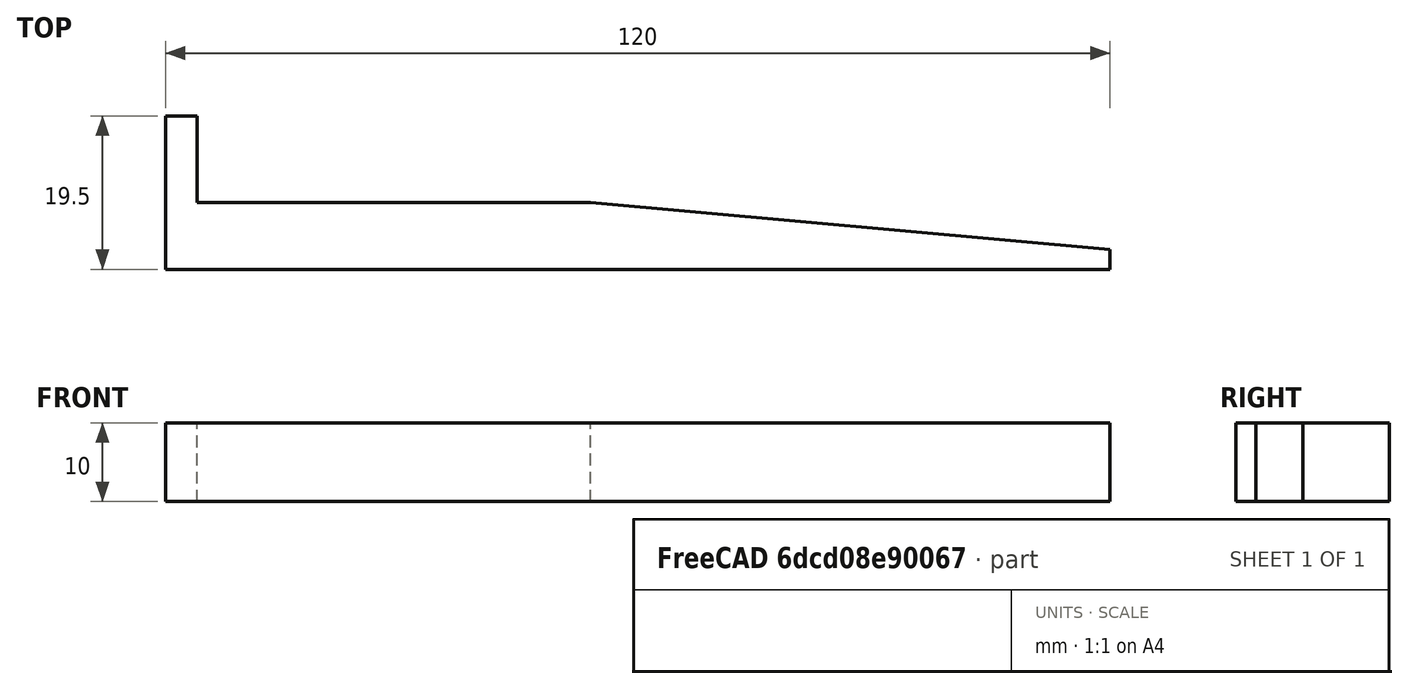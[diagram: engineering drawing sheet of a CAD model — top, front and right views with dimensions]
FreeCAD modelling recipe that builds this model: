
FCSTD DOCUMENT  (FreeCAD 0.21R33668 +7 (Git))
Label: locking plug
License: All rights reserved
LicenseURL: http://en.wikipedia.org/wiki/All_rights_reserved
objects: Sketcher::SketchObject×1, PartDesign::Pad×1, PartDesign::Body×1
note: 4 computed .brp shape members not serialized (recipe doc carries the construction recipe); baked Part::Feature solids carry a one-line shape summary decoded from their .brp

FEATURE [Sketcher::SketchObject] Sketch
  FullyConstrained = true
  MapMode = 5
  Support = -> [XY_Plane]
  sketch-geometry (7):
    g0: LineSegment StartX=0 StartY=0 StartZ=0 EndX=0 EndY=19.5 EndZ=0
    g1: LineSegment StartX=0 StartY=19.5 StartZ=0 EndX=4 EndY=19.5 EndZ=0
    g2: LineSegment StartX=4 StartY=19.5 StartZ=0 EndX=4 EndY=8.5 EndZ=0
    g3: LineSegment StartX=4 StartY=8.5 StartZ=0 EndX=54 EndY=8.5 EndZ=0
    g4: LineSegment StartX=54 StartY=8.5 StartZ=0 EndX=120 EndY=2.51 EndZ=0
    g5: LineSegment StartX=120 StartY=2.51 StartZ=0 EndX=120 EndY=0 EndZ=0
    g6: LineSegment StartX=120 StartY=0 StartZ=0 EndX=0 EndY=0 EndZ=0
  constraints (20):
    c: Coincident(g-1,g0)
    c: PointOnObject(g0,g-2)
    c: Coincident(g0,g1)
    c: Horizontal(g1)
    c: Coincident(g1,g2)
    c: Vertical(g2)
    c: Coincident(g2,g3)
    c: Horizontal(g3)
    c: Coincident(g3,g4)
    c: Coincident(g4,g5)
    c: PointOnObject(g5,g-1)
    c: Coincident(g5,g6)
    c: Coincident(g6,g0)
    c: Vertical(g5)
    c: DistanceX(g1,g1) = 4
    c: DistanceY(g0,g0) = 19.5
    c: DistanceY(g2,g2) = 11
    c: DistanceX(g3,g3) = 50
    c: DistanceX(g6,g6) = 120
    c: DistanceY(g5,g5) = 2.51
FEATURE [PartDesign::Pad] Pad
  Direction = (0,0,1)
  Length = 10
  Length2 = 10
  Profile = -> Sketch
  ReferenceAxis = -> Sketch [N_Axis]
  Type = 0
FEATURE [PartDesign::Body] Body
  Group = -> [Sketch,Pad]
  Origin = -> Origin
  Tip = -> Pad
